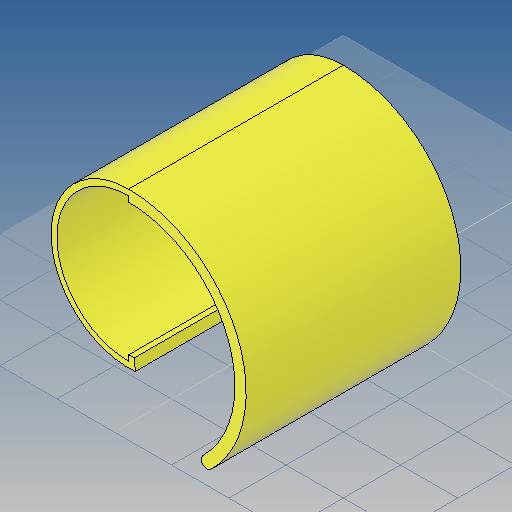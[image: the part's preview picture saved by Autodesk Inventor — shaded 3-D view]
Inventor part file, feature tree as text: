
AUTODESK INVENTOR PART (.ipt)
format: ipt  version: 2019 (Build 230136000, 136)  size: 147,968 bytes
history: native  units: mm
features: other x1, sketch x1, extrude x1
ambient origin geometry x8: Origin, YZ Plane, XZ Plane, XY Plane, X Axis, Y Axis, Z Axis, Center Point
bodies: Volumenkörper1 (feature_tree)
feature tree (3):
  other  "<userpath>\OneDrive\Dokumente\Inventor\Absauganlage\Absauganlage_Params.xlsx"
  sketch  "Skizze1"  dims[d0=50.1mm d2=46.2mm d3=2.0mm d4=0.872665mm d6=75.0mm d7=0.0mm d11=25.0mm d12=15.0mm d16=1.0mm]
  extrude  "Extrusion1"  Depth=75.0mm
